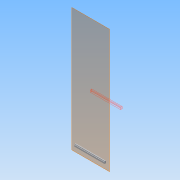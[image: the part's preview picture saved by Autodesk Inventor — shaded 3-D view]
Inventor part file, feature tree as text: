
AUTODESK INVENTOR PART (.ipt)
format: ipt  version: 2013 (Build 170138000, 138)  size: 76,800 bytes
history: native  units: in
note: dims shown in document units (in); Inventor stores cm internally (conversion verified against a paired STEP export)
features: extrude x2, sketch x2, plane x1
ambient origin geometry x8: Origin, YZ Plane, XZ Plane, XY Plane, X Axis, Y Axis, Z Axis, Center Point
bodies: Solid1 (feature_tree)
feature tree (5):
  plane  "Work Plane1"
  extrude  "Extrusion1"  Depth=1.5in
  extrude  "Extrusion2"  Depth=0.5in
  sketch  "Sketch1"  dims[d0=20.8125in d1=1.5in]
  sketch  "Sketch2"  dims[d2=1.0in d3=0.0in d4=0.5in d5=0.3332in d6=0.0in]
